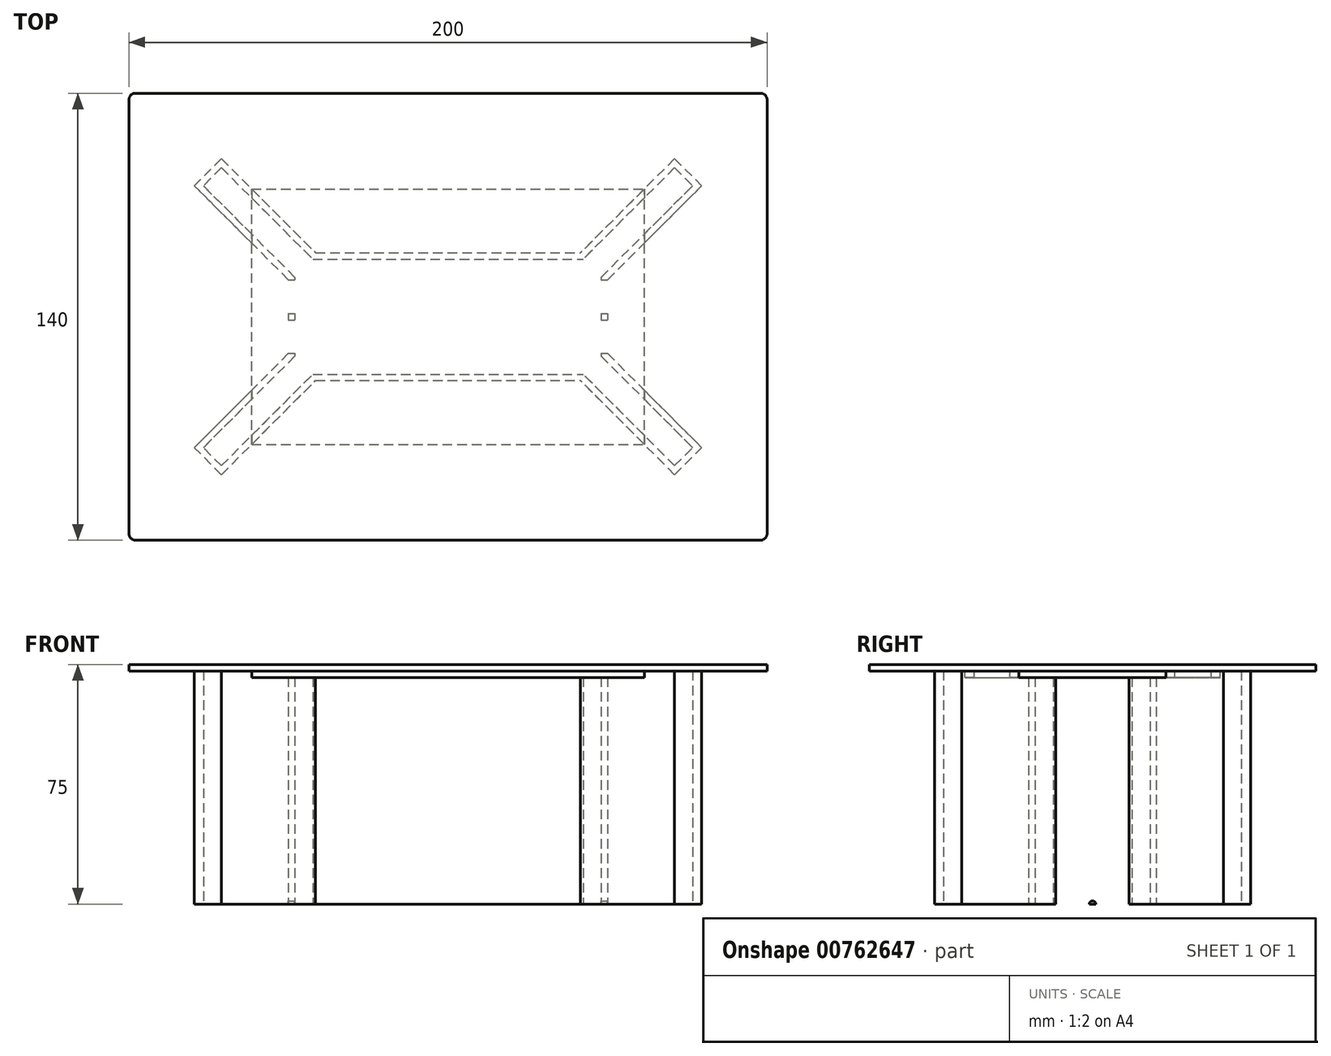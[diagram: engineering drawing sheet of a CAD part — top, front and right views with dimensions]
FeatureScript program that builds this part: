
annotation { "Feature Type Name" : "Feature", "Feature Type Description" : "" }
export const myFeature = defineFeature(function(context is Context, id is Id, definition is map)
    precondition{}
    {
        {
            var Q0;
            Q0=qCreatedBy(makeId("Top.planeOp"),FACE);
            cPlane(context, id + "F0", {"entities" : qUnion([Q0]), "cplaneType" : CPlaneType.OFFSET, "offset" : 73 * mm, "width" : 150 * mm, "height" : 150 * mm});
        }
        {
            var Q0;
            Q0=qCreatedBy(id+"F0.planeOp",FACE);
            var sketch = newSketch(context, id + "F1", { "sketchPlane" : qUnion([Q0])});
            skLineSegment(sketch, "E0.bottom", {"start": v(-98, 70) * mm, "end": v(98, 70) * mm});
            skLineSegment(sketch, "E0.top", {"start": v(-98, -70) * mm, "end": v(98, -70) * mm});
            skLineSegment(sketch, "E0.left", {"start": v(-100, 68) * mm, "end": v(-100, -68) * mm});
            skLineSegment(sketch, "E0.right", {"start": v(100, 68) * mm, "end": v(100, -68) * mm});
            skPoint(sketch, "E1.visualSharp", {"position": v(-100, -70) * mm});
            skArc(sketch, "E1.filletArc", {"start": v(-100, -68) * mm, "mid": v(-99.41, -69.41) * mm, "end": v(-98, -70) * mm});
            skPoint(sketch, "E2.visualSharp", {"position": v(100, -70) * mm});
            skArc(sketch, "E2.filletArc", {"start": v(98, -70) * mm, "mid": v(99.41, -69.41) * mm, "end": v(100, -68) * mm});
            skPoint(sketch, "E3.visualSharp", {"position": v(100, 70) * mm});
            skArc(sketch, "E3.filletArc", {"start": v(100, 68) * mm, "mid": v(99.41, 69.41) * mm, "end": v(98, 70) * mm});
            skPoint(sketch, "E4.visualSharp", {"position": v(-100, 70) * mm});
            skArc(sketch, "E4.filletArc", {"start": v(-98, 70) * mm, "mid": v(-99.41, 69.41) * mm, "end": v(-100, 68) * mm});
            skSolve(sketch);
        }
        {
            var Q0;
            Q0=makeQuery(id+"F1.imprint","IMPRINT",FACE,{"disambiguationData":[TD([[makeQuery(id+"F1.imprint","IMPRINT",EDGE,{"derivedFrom":sQuery(id+"F1.wireOp",EDGE,"E0.bottom")}),-1.0]])]});
            extrude(context, id + "F2", {"entities" : qUnion([Q0]), "depth" : 2 * mm, "offsetDistance" : 25 * mm});
        }
        {
            var Q0;
            Q0=qCreatedBy(makeId("Top.planeOp"),FACE);
            var sketch = newSketch(context, id + "F3", { "sketchPlane" : qUnion([Q0])});
            skLineSegment(sketch, "E5.bottom", {"start": v(-100, 70) * mm, "end": v(100, 70) * mm, "construction": true});
            skLineSegment(sketch, "E5.top", {"start": v(-100, -70) * mm, "end": v(100, -70) * mm, "construction": true});
            skLineSegment(sketch, "E5.left", {"start": v(-100, 70) * mm, "end": v(-100, -70) * mm, "construction": true});
            skLineSegment(sketch, "E5.right", {"start": v(100, 70) * mm, "end": v(100, -70) * mm, "construction": true});
            skLineSegment(sketch, "E6.0", {"start": v(-50, 20) * mm, "end": v(-50, -20) * mm, "construction": true});
            skLineSegment(sketch, "E7.0", {"start": v(-50, 20) * mm, "end": v(50, 20) * mm, "construction": true});
            skLineSegment(sketch, "E8.0", {"start": v(50, 20) * mm, "end": v(50, -20) * mm, "construction": true});
            skLineSegment(sketch, "E9.0", {"start": v(-50, -20) * mm, "end": v(50, -20) * mm, "construction": true});
            skLineSegment(sketch, "E10.0", {"start": v(-70, 40) * mm, "end": v(70, 40) * mm, "construction": true});
            skLineSegment(sketch, "E11.0", {"start": v(70, 40) * mm, "end": v(70, -40) * mm, "construction": true});
            skLineSegment(sketch, "E12.0", {"start": v(-70, -40) * mm, "end": v(70, -40) * mm, "construction": true});
            skLineSegment(sketch, "E13.0", {"start": v(-70, 40) * mm, "end": v(-70, -40) * mm, "construction": true});
            skLineSegment(sketch, "E14", {"start": v(-50, 20) * mm, "end": v(-100, 70) * mm, "construction": true});
            skLineSegment(sketch, "E15", {"start": v(-50, -20) * mm, "end": v(-100, -70) * mm, "construction": true});
            skLineSegment(sketch, "E16", {"start": v(50, 20) * mm, "end": v(100, 70) * mm, "construction": true});
            skLineSegment(sketch, "E17", {"start": v(50, -20) * mm, "end": v(100, -70) * mm, "construction": true});
            skSolve(sketch);
        }
        {
            var Q0;
            Q0=qCreatedBy(makeId("Top.planeOp"),FACE);
            var sketch = newSketch(context, id + "F4", { "sketchPlane" : qUnion([Q0])});
            skLineSegment(sketch, "E18.bottom", {"start": v(-41.51, 20) * mm, "end": v(41.51, 20) * mm});
            skLineSegment(sketch, "E18.top", {"start": v(-41.51, -20) * mm, "end": v(41.51, -20) * mm});
            skLineSegment(sketch, "E18.right", {"start": v(50, 11.51) * mm, "end": v(50, -11.51) * mm});
            skLineSegment(sketch, "E19", {"start": v(-50, 11.51) * mm, "end": v(-50, -11.51) * mm});
            skLineSegment(sketch, "E20", {"start": v(-71, 49.5) * mm, "end": v(-41.51, 20) * mm});
            skLineSegment(sketch, "E21", {"start": v(-50, 11.51) * mm, "end": v(-79.5, 41) * mm});
            skLineSegment(sketch, "E22", {"start": v(-71, 49.5) * mm, "end": v(-79.5, 41) * mm});
            skLineSegment(sketch, "E23.MirrorCS", {"start": v(71, 49.5) * mm, "end": v(41.51, 20) * mm});
            skLineSegment(sketch, "E24.MirrorCS", {"start": v(71, 49.5) * mm, "end": v(79.5, 41) * mm});
            skLineSegment(sketch, "E25.MirrorCS", {"start": v(50, 11.51) * mm, "end": v(79.5, 41) * mm});
            skLineSegment(sketch, "E26.MirrorCS", {"start": v(50, -11.51) * mm, "end": v(79.5, -41) * mm});
            skLineSegment(sketch, "E27.MirrorCS", {"start": v(71, -49.5) * mm, "end": v(41.51, -20) * mm});
            skLineSegment(sketch, "E28.MirrorCS", {"start": v(71, -49.5) * mm, "end": v(79.5, -41) * mm});
            skLineSegment(sketch, "E29.MirrorCS", {"start": v(-71, -49.5) * mm, "end": v(-41.51, -20) * mm});
            skLineSegment(sketch, "E30.MirrorCS", {"start": v(-50, -11.51) * mm, "end": v(-79.5, -41) * mm});
            skLineSegment(sketch, "E31.MirrorCS", {"start": v(-71, -49.5) * mm, "end": v(-79.5, -41) * mm});
            skLineSegment(sketch, "E32.0", {"start": v(-71, 46.67) * mm, "end": v(-42.34, 18) * mm});
            skLineSegment(sketch, "E33.0", {"start": v(-71, 46.67) * mm, "end": v(-76.67, 41) * mm});
            skLineSegment(sketch, "E34.0", {"start": v(-48, 12.34) * mm, "end": v(-76.67, 41) * mm});
            skLineSegment(sketch, "E35.0", {"start": v(-48, 12.34) * mm, "end": v(-48, -12.34) * mm});
            skLineSegment(sketch, "E36.0", {"start": v(-42.34, 18) * mm, "end": v(42.34, 18) * mm});
            skLineSegment(sketch, "E37.MirrorCS", {"start": v(71, 46.67) * mm, "end": v(42.34, 18) * mm});
            skLineSegment(sketch, "E38.MirrorCS", {"start": v(48, 12.34) * mm, "end": v(76.67, 41) * mm});
            skLineSegment(sketch, "E39.MirrorCS", {"start": v(71, 46.67) * mm, "end": v(76.67, 41) * mm});
            skLineSegment(sketch, "E40.MirrorCS", {"start": v(48, 12.34) * mm, "end": v(48, -12.34) * mm});
            skLineSegment(sketch, "E41.MirrorCS", {"start": v(-71, -46.67) * mm, "end": v(-42.34, -18) * mm});
            skLineSegment(sketch, "E42.MirrorCS", {"start": v(-48, -12.34) * mm, "end": v(-76.67, -41) * mm});
            skLineSegment(sketch, "E43.MirrorCS", {"start": v(-71, -46.67) * mm, "end": v(-76.67, -41) * mm});
            skLineSegment(sketch, "E44.MirrorCS", {"start": v(-42.34, -18) * mm, "end": v(42.34, -18) * mm});
            skLineSegment(sketch, "E45.MirrorCS", {"start": v(48, -12.34) * mm, "end": v(76.67, -41) * mm});
            skLineSegment(sketch, "E46.MirrorCS", {"start": v(71, -46.67) * mm, "end": v(42.34, -18) * mm});
            skLineSegment(sketch, "E47.MirrorCS", {"start": v(71, -46.67) * mm, "end": v(76.67, -41) * mm});
            skSolve(sketch);
        }
        {
            var Q0;
            Q0 = qSketchRegion(id + "F4", true);
            var Q1;
            Q1=qCreatedBy(id+"F0.planeOp",FACE);
            extrude(context, id + "F5", {"entities" : qUnion([Q0]), "endBound" : BoundingType.UP_TO_SURFACE, "depth" : 25 * mm, "endBoundEntityFace" : qUnion([Q1]), "offsetDistance" : 25 * mm});
        }
        {
            var Q0;
            Q0=qCreatedBy(id+"F0.planeOp",FACE);
            var sketch = newSketch(context, id + "F6", { "sketchPlane" : qUnion([Q0])});
            skLineSegment(sketch, "E48.bottom", {"start": v(61.51, 40) * mm, "end": v(-61.51, 40) * mm});
            skLineSegment(sketch, "E48.top", {"start": v(61.51, -40) * mm, "end": v(-61.51, -40) * mm});
            skLineSegment(sketch, "E49", {"start": v(-61.51, 40) * mm, "end": v(-61.51, -40) * mm});
            skLineSegment(sketch, "E50", {"start": v(61.51, 40) * mm, "end": v(61.51, -40) * mm});
            skSolve(sketch);
        }
        {
            var Q0;
            Q0 = qSketchRegion(id + "F6", true);
            extrude(context, id + "F7", {"entities" : qUnion([Q0]), "oppositeDirection" : true, "depth" : 2 * mm, "offsetDistance" : 25 * mm});
        }
        {
            var Q0;
            Q0=makeQuery(id+"F7.opExtrude","SWEPT_BODY",BODY,{"disambiguationData":[OSD([sQuery(id+"F6.wireOp",EDGE,"E48.bottom"),sQuery(id+"F6.wireOp",EDGE,"E48.top"),sQuery(id+"F6.wireOp",EDGE,"E49"),sQuery(id+"F6.wireOp",EDGE,"E50")])]});
            var Q1;
            Q1=makeQuery(id+"F5.opExtrude","SWEPT_BODY",BODY,{"disambiguationData":[OSD([sQuery(id+"F4.wireOp",EDGE,"E18.bottom"),sQuery(id+"F4.wireOp",EDGE,"E18.top"),sQuery(id+"F4.wireOp",EDGE,"E18.right"),sQuery(id+"F4.wireOp",EDGE,"E19"),sQuery(id+"F4.wireOp",EDGE,"E20"),sQuery(id+"F4.wireOp",EDGE,"E21"),sQuery(id+"F4.wireOp",EDGE,"E22"),sQuery(id+"F4.wireOp",EDGE,"E23.MirrorCS"),sQuery(id+"F4.wireOp",EDGE,"E24.MirrorCS"),sQuery(id+"F4.wireOp",EDGE,"E25.MirrorCS"),sQuery(id+"F4.wireOp",EDGE,"E26.MirrorCS"),sQuery(id+"F4.wireOp",EDGE,"E27.MirrorCS"),sQuery(id+"F4.wireOp",EDGE,"E28.MirrorCS"),sQuery(id+"F4.wireOp",EDGE,"E29.MirrorCS"),sQuery(id+"F4.wireOp",EDGE,"E30.MirrorCS"),sQuery(id+"F4.wireOp",EDGE,"E31.MirrorCS"),sQuery(id+"F4.wireOp",EDGE,"E32.0"),sQuery(id+"F4.wireOp",EDGE,"E33.0"),sQuery(id+"F4.wireOp",EDGE,"E34.0"),sQuery(id+"F4.wireOp",EDGE,"E35.0"),sQuery(id+"F4.wireOp",EDGE,"E36.0"),sQuery(id+"F4.wireOp",EDGE,"E37.MirrorCS"),sQuery(id+"F4.wireOp",EDGE,"E38.MirrorCS"),sQuery(id+"F4.wireOp",EDGE,"E39.MirrorCS"),sQuery(id+"F4.wireOp",EDGE,"E40.MirrorCS"),sQuery(id+"F4.wireOp",EDGE,"E41.MirrorCS"),sQuery(id+"F4.wireOp",EDGE,"E42.MirrorCS"),sQuery(id+"F4.wireOp",EDGE,"E43.MirrorCS"),sQuery(id+"F4.wireOp",EDGE,"E44.MirrorCS"),sQuery(id+"F4.wireOp",EDGE,"E45.MirrorCS"),sQuery(id+"F4.wireOp",EDGE,"E46.MirrorCS"),sQuery(id+"F4.wireOp",EDGE,"E47.MirrorCS")])]});
            booleanBodies(context, id + "F8", {"operationType" : BooleanOperationType.SUBTRACTION, "tools" : qUnion([Q0]), "targets" : qUnion([Q1])});
        }
        {
            var Q0;
            Q0 = qSketchRegion(id + "F6", true);
            var Q1;
            {var subQ0=sQuery(id+"F6.wireOp",EDGE,"E49");Q1=makeQuery(id+"F8.opBoolean","COPY",FACE,{"disambiguationData":[TD([makeQuery(id+"F5.opExtrude","SWEPT_FACE",FACE,{"disambiguationData":[OSD([sQuery(id+"F4.wireOp",EDGE,"E19")])]})])],"derivedFrom":makeQuery(id+"F7.opExtrude","CAP_FACE",FACE,{"disambiguationData":[OSD([sQuery(id+"F6.wireOp",EDGE,"E48.bottom"),sQuery(id+"F6.wireOp",EDGE,"E48.top"),subQ0,sQuery(id+"F6.wireOp",EDGE,"E50")])],"isStart":false})});}
            extrude(context, id + "F9", {"entities" : qUnion([Q0]), "endBound" : BoundingType.UP_TO_SURFACE, "oppositeDirection" : true, "depth" : 25 * mm, "endBoundEntityFace" : qUnion([Q1]), "offsetDistance" : 25 * mm});
        }
        {
            var Q0;
            Q0=makeQuery(id+"F5.opExtrude","SWEPT_FACE",FACE,{"disambiguationData":[OSD([sQuery(id+"F4.wireOp",EDGE,"E19")])]});
            var sketch = newSketch(context, id + "F10", { "sketchPlane" : qUnion([Q0])});
            skLineSegment(sketch, "E51.bottom", {"start": v(-9, 50) * mm, "end": v(9, 50) * mm});
            skLineSegment(sketch, "E51.top", {"start": v(-9, 20) * mm, "end": v(9, 20) * mm});
            skLineSegment(sketch, "E51.left", {"start": v(-9, 50) * mm, "end": v(-9, 20) * mm});
            skLineSegment(sketch, "E51.right", {"start": v(9, 50) * mm, "end": v(9, 20) * mm});
            skSolve(sketch);
        }
        {
            var Q0;
            Q0=makeQuery(id+"F10.imprint","IMPRINT",FACE,{"disambiguationData":[TD([[makeQuery(id+"F10.imprint","IMPRINT",EDGE,{"derivedFrom":sQuery(id+"F10.wireOp",EDGE,"E51.bottom")}),-1.0]])]});
            extrude(context, id + "F11", {"entities" : qUnion([Q0]), "operationType" : NewBodyOperationType.REMOVE, "endBound" : BoundingType.THROUGH_ALL, "oppositeDirection" : true, "depth" : 5 * mm, "offsetDistance" : 25 * mm});
        }
        {
            var Q0;
            Q0=makeQuery(id+"F5.opExtrude","SWEPT_FACE",FACE,{"disambiguationData":[OSD([sQuery(id+"F4.wireOp",EDGE,"E18.right")])]});
            var sketch = newSketch(context, id + "F12", { "sketchPlane" : qUnion([Q0])});
            skLineSegment(sketch, "E52.bottom", {"start": v(-6.1, 65) * mm, "end": v(6.1, 65) * mm});
            skLineSegment(sketch, "E52.top", {"start": v(-6.1, 59.8) * mm, "end": v(6.1, 59.8) * mm});
            skLineSegment(sketch, "E52.left", {"start": v(-6.1, 65) * mm, "end": v(-6.1, 59.8) * mm});
            skLineSegment(sketch, "E52.right", {"start": v(6.1, 65) * mm, "end": v(6.1, 59.8) * mm});
            skSolve(sketch);
        }
        {
            var Q0;
            Q0=makeQuery(id+"F12.imprint","IMPRINT",FACE,{"disambiguationData":[TD([[makeQuery(id+"F12.imprint","IMPRINT",EDGE,{"derivedFrom":sQuery(id+"F12.wireOp",EDGE,"E52.bottom")}),-1.0]])]});
            extrude(context, id + "F13", {"entities" : qUnion([Q0]), "operationType" : NewBodyOperationType.REMOVE, "endBound" : BoundingType.THROUGH_ALL, "oppositeDirection" : true, "depth" : 25 * mm, "offsetDistance" : 25 * mm});
        }
        {
            var Q0;
            Q0=makeQuery(id+"F5.opExtrude","SWEPT_FACE",FACE,{"disambiguationData":[OSD([sQuery(id+"F4.wireOp",EDGE,"E18.right")])]});
            var sketch = newSketch(context, id + "F14", { "sketchPlane" : qUnion([Q0])});
            skArc(sketch, "E53", {"start": v(-1, 0) * mm, "mid": v(0, 1) * mm, "end": v(1, 0) * mm});
            skLineSegment(sketch, "E54", {"start": v(-1, 0) * mm, "end": v(1, 0) * mm});
            skSolve(sketch);
        }
        {
            var Q0;
            Q0=makeQuery(id+"F14.imprint","IMPRINT",FACE,{"disambiguationData":[TD([[makeQuery(id+"F14.imprint","IMPRINT",EDGE,{"derivedFrom":sQuery(id+"F14.wireOp",EDGE,"E53")}),-1.0]])]});
            extrude(context, id + "F15", {"entities" : qUnion([Q0]), "operationType" : NewBodyOperationType.REMOVE, "endBound" : BoundingType.THROUGH_ALL, "oppositeDirection" : true, "depth" : 25 * mm, "offsetDistance" : 25 * mm});
        }
    });
